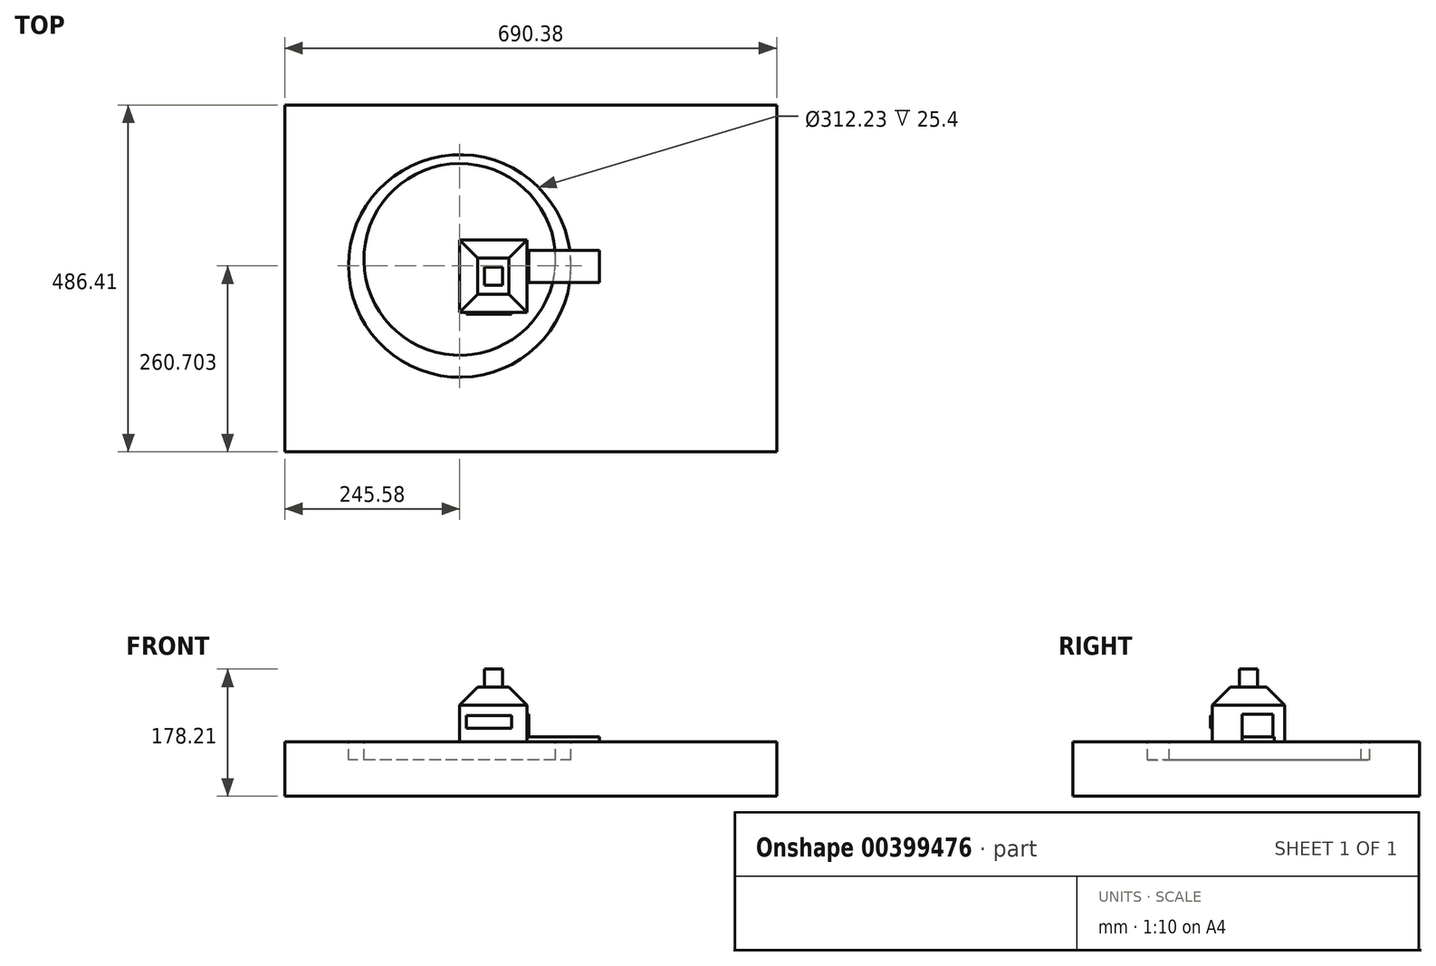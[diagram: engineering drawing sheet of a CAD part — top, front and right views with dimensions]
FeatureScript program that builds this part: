
annotation { "Feature Type Name" : "Feature", "Feature Type Description" : "" }
export const myFeature = defineFeature(function(context is Context, id is Id, definition is map)
    precondition{}
    {
        {
            var Q0;
            Q0=qCreatedBy(makeId("Front.planeOp"),FACE);
            var sketch = newSketch(context, id + "F0", { "sketchPlane" : qUnion([Q0])});
            skLineSegment(sketch, "E0.bottom", {"start": v(0, 0) * mm, "end": v(94.42, 0) * mm});
            skLineSegment(sketch, "E0.top", {"start": v(0, 76.6) * mm, "end": v(94.42, 76.6) * mm});
            skLineSegment(sketch, "E0.left", {"start": v(0, 0) * mm, "end": v(0, 76.6) * mm});
            skLineSegment(sketch, "E0.right", {"start": v(94.42, 0) * mm, "end": v(94.42, 76.6) * mm});
            skSolve(sketch);
        }
        {
            var Q0;
            Q0=makeQuery(id+"F0.imprint","IMPRINT",FACE,{"disambiguationData":[TD([[makeQuery(id+"F0.imprint","IMPRINT",EDGE,{"derivedFrom":sQuery(id+"F0.wireOp",EDGE,"E0.bottom")}),1.0]])]});
            extrude(context, id + "F1", {"entities" : qUnion([Q0]), "depth" : 101.6 * mm});
        }
        {
            var Q0;
            Q0=makeQuery(id+"F1.opExtrude","SWEPT_FACE",FACE,{"disambiguationData":[OSD([sQuery(id+"F0.wireOp",EDGE,"E0.top")])]});
            chamfer(context, id + "F2", {"entities" : qUnion([Q0]), "width" : 25.4 * mm, "tangentPropagation" : true});
        }
        {
            var Q0;
            Q0=makeQuery(id+"F1.opExtrude","SWEPT_FACE",FACE,{"disambiguationData":[OSD([sQuery(id+"F0.wireOp",EDGE,"E0.top")])]});
            var sketch = newSketch(context, id + "F3", { "sketchPlane" : qUnion([Q0])});
            skLineSegment(sketch, "E1.bottom", {"start": v(34.5, -63.5) * mm, "end": v(59.9, -63.5) * mm});
            skLineSegment(sketch, "E1.top", {"start": v(34.5, -38.1) * mm, "end": v(59.9, -38.1) * mm});
            skLineSegment(sketch, "E1.left", {"start": v(34.5, -63.5) * mm, "end": v(34.5, -38.1) * mm});
            skLineSegment(sketch, "E1.right", {"start": v(59.9, -63.5) * mm, "end": v(59.9, -38.1) * mm});
            skSolve(sketch);
        }
        {
            var Q0;
            Q0=makeQuery(id+"F3.imprint","IMPRINT",FACE,{"disambiguationData":[TD([[makeQuery(id+"F3.imprint","IMPRINT",EDGE,{"derivedFrom":sQuery(id+"F3.wireOp",EDGE,"E1.bottom")}),1.0]])]});
            extrude(context, id + "F4", {"entities" : qUnion([Q0]), "operationType" : NewBodyOperationType.ADD, "depth" : 25.4 * mm});
        }
        {
            var Q0;
            Q0=makeQuery(id+"F1.opExtrude","CAP_FACE",FACE,{"disambiguationData":[OSD([sQuery(id+"F0.wireOp",EDGE,"E0.bottom"),sQuery(id+"F0.wireOp",EDGE,"E0.top"),sQuery(id+"F0.wireOp",EDGE,"E0.left"),sQuery(id+"F0.wireOp",EDGE,"E0.right")])],"isStart":false});
            var sketch = newSketch(context, id + "F5", { "sketchPlane" : qUnion([Q0])});
            skLineSegment(sketch, "E2.bottom", {"start": v(9.13, 36.58) * mm, "end": v(72.87, 36.58) * mm});
            skLineSegment(sketch, "E2.top", {"start": v(9.13, 18.94) * mm, "end": v(72.87, 18.94) * mm});
            skLineSegment(sketch, "E2.left", {"start": v(9.13, 36.58) * mm, "end": v(9.13, 18.94) * mm});
            skLineSegment(sketch, "E2.right", {"start": v(72.87, 36.58) * mm, "end": v(72.87, 18.94) * mm});
            skSolve(sketch);
        }
        {
            var Q0;
            Q0=makeQuery(id+"F1.opExtrude","SWEPT_FACE",FACE,{"disambiguationData":[OSD([sQuery(id+"F0.wireOp",EDGE,"E0.right")])]});
            var sketch = newSketch(context, id + "F6", { "sketchPlane" : qUnion([Q0])});
            skLineSegment(sketch, "E3.bottom", {"start": v(-59.73, 0) * mm, "end": v(-14.6, 0) * mm});
            skLineSegment(sketch, "E3.top", {"start": v(-59.73, 6.8) * mm, "end": v(-14.6, 6.8) * mm});
            skLineSegment(sketch, "E3.left", {"start": v(-59.73, 0) * mm, "end": v(-59.73, 6.8) * mm});
            skLineSegment(sketch, "E3.right", {"start": v(-14.6, 0) * mm, "end": v(-14.6, 6.8) * mm});
            skSolve(sketch);
        }
        {
            var Q0;
            Q0=makeQuery(id+"F6.imprint","IMPRINT",FACE,{"disambiguationData":[TD([[makeQuery(id+"F6.imprint","IMPRINT",EDGE,{"derivedFrom":sQuery(id+"F6.wireOp",EDGE,"E3.bottom")}),1.0]])]});
            extrude(context, id + "F7", {"entities" : qUnion([Q0]), "operationType" : NewBodyOperationType.ADD, "depth" : 101.6 * mm});
        }
        {
            var Q0;
            Q0=makeQuery(id+"F5.imprint","IMPRINT",FACE,{"disambiguationData":[TD([[makeQuery(id+"F5.imprint","IMPRINT",EDGE,{"derivedFrom":sQuery(id+"F5.wireOp",EDGE,"E2.bottom")}),-1.0]])]});
            extrude(context, id + "F8", {"entities" : qUnion([Q0]), "operationType" : NewBodyOperationType.ADD, "depth" : 2.54 * mm});
        }
        {
            var Q0;
            Q0=makeQuery(id+"F1.opExtrude","SWEPT_FACE",FACE,{"disambiguationData":[OSD([sQuery(id+"F0.wireOp",EDGE,"E0.right")])]});
            var sketch = newSketch(context, id + "F9", { "sketchPlane" : qUnion([Q0])});
            skLineSegment(sketch, "E4.bottom", {"start": v(-59.73, 6.8) * mm, "end": v(-16.32, 6.8) * mm});
            skLineSegment(sketch, "E4.top", {"start": v(-59.73, 38.95) * mm, "end": v(-16.32, 38.95) * mm});
            skLineSegment(sketch, "E4.left", {"start": v(-59.73, 6.8) * mm, "end": v(-59.73, 38.95) * mm});
            skLineSegment(sketch, "E4.right", {"start": v(-16.32, 6.8) * mm, "end": v(-16.32, 38.95) * mm});
            skSolve(sketch);
        }
        {
            var Q0;
            Q0=makeQuery(id+"F9.imprint","IMPRINT",FACE,{"disambiguationData":[TD([[makeQuery(id+"F9.imprint","IMPRINT",EDGE,{"derivedFrom":sQuery(id+"F9.wireOp",EDGE,"E4.bottom")}),1.0]])]});
            extrude(context, id + "F10", {"entities" : qUnion([Q0]), "operationType" : NewBodyOperationType.ADD, "depth" : 2.54 * mm});
        }
        {
            var Q0;
            Q0=makeQuery(id+"F7.boolean.opBoolean","MERGE",FACE,{"derivedFrom":[makeQuery(id+"F1.opExtrude","SWEPT_FACE",FACE,{"disambiguationData":[OSD([sQuery(id+"F0.wireOp",EDGE,"E0.bottom")])]}),makeQuery(id+"F7.opExtrude","SWEPT_FACE",FACE,{"disambiguationData":[OSD([sQuery(id+"F6.wireOp",EDGE,"E3.bottom")])]})]});
            var sketch = newSketch(context, id + "F11", { "sketchPlane" : qUnion([Q0])});
            skLineSegment(sketch, "E5.bottom", {"start": v(-245.58, 297.2) * mm, "end": v(444.8, 297.2) * mm});
            skLineSegment(sketch, "E5.top", {"start": v(-245.58, -189.22) * mm, "end": v(444.8, -189.22) * mm});
            skLineSegment(sketch, "E5.left", {"start": v(-245.58, 297.2) * mm, "end": v(-245.58, -189.22) * mm});
            skLineSegment(sketch, "E5.right", {"start": v(444.8, 297.2) * mm, "end": v(444.8, -189.22) * mm});
            skSolve(sketch);
        }
        {
            var Q0;
            Q0=makeQuery(id+"F11.imprint","IMPRINT",FACE,{"disambiguationData":[TD([[makeQuery(id+"F11.imprint","IMPRINT",EDGE,{"derivedFrom":sQuery(id+"F11.wireOp",EDGE,"E5.bottom")}),-1.0]])]});
            var Q1;
            {var subQ3=sQuery(id+"F0.wireOp",EDGE,"E0.bottom");Q1=makeQuery(id+"F11.imprint","IMPRINT",FACE,{"disambiguationData":[TD([[makeQuery(id+"F11.imprint","IMPRINT",EDGE,{"derivedFrom":makeQuery(id+"F1.opExtrude","CAP_EDGE",EDGE,{"disambiguationData":[OSD([subQ3])],"isStart":true})}),1.0]])]});}
            extrude(context, id + "F12", {"entities" : qUnion([Q0, Q1]), "operationType" : NewBodyOperationType.ADD, "depth" : 76.2 * mm});
        }
        {
            var Q0;
            Q0=makeQuery(id+"F12.opExtrude","CAP_FACE",FACE,{"disambiguationData":[OSD([sQuery(id+"F11.wireOp",EDGE,"E5.bottom"),sQuery(id+"F11.wireOp",EDGE,"E5.top"),sQuery(id+"F11.wireOp",EDGE,"E5.left"),sQuery(id+"F11.wireOp",EDGE,"E5.right")])],"isStart":true});
            var sketch = newSketch(context, id + "F13", { "sketchPlane" : qUnion([Q0])});
            skLineSegment(sketch, "E6.bottom", {"start": v(444.8, -297.2) * mm, "end": v(194.55, -297.2) * mm});
            skLineSegment(sketch, "E6.top", {"start": v(444.8, 189.22) * mm, "end": v(194.55, 189.22) * mm});
            skLineSegment(sketch, "E6.left", {"start": v(444.8, -297.2) * mm, "end": v(444.8, 189.22) * mm});
            skLineSegment(sketch, "E6.right", {"start": v(194.55, -297.2) * mm, "end": v(194.55, 189.22) * mm});
            skSolve(sketch);
        }
        {
            var Q0;
            {var subQ11=makeQuery(id+"F12.opExtrude","CAP_EDGE",EDGE,{"disambiguationData":[OSD([sQuery(id+"F11.wireOp",EDGE,"E5.left")])],"isStart":true});Q0=makeQuery(id+"F13.imprint","IMPRINT",FACE,{"disambiguationData":[TD([[makeQuery(id+"F13.imprint","IMPRINT",EDGE,{"derivedFrom":subQ11}),-1.0]])]});}
            var sketch = newSketch(context, id + "F14", { "sketchPlane" : qUnion([Q0])});
            skCircle(sketch, "E7", {"center": v(0, -36.49) * mm, "radius": 156.11 * mm});
            skSolve(sketch);
        }
        {
            var Q0;
            Q0 = qSketchRegion(id + "F14", true);
            extrude(context, id + "F15", {"entities" : qUnion([Q0]), "operationType" : NewBodyOperationType.REMOVE, "oppositeDirection" : true, "depth" : 25.4 * mm});
        }
        {
            var Q0;
            {var subQ11=makeQuery(id+"F12.opExtrude","CAP_EDGE",EDGE,{"disambiguationData":[OSD([sQuery(id+"F11.wireOp",EDGE,"E5.left")])],"isStart":true});Q0=makeQuery(id+"F13.imprint","IMPRINT",FACE,{"disambiguationData":[TD([[makeQuery(id+"F13.imprint","IMPRINT",EDGE,{"derivedFrom":subQ11}),-1.0]])]});}
            var sketch = newSketch(context, id + "F16", { "sketchPlane" : qUnion([Q0])});
            skCircle(sketch, "E8", {"center": v(0, -27.2) * mm, "radius": 134.47 * mm});
            skSolve(sketch);
        }
        {
            var Q0;
            Q0 = qSketchRegion(id + "F16", true);
            var Q1;
            Q1=makeQuery(id+"F15.boolean.opBoolean","COPY",FACE,{"derivedFrom":makeQuery(id+"F15.opExtrude","CAP_FACE",FACE,{"disambiguationData":[OSD([sQuery(id+"F14.wireOp",EDGE,"E7")])],"isStart":false})});
            extrude(context, id + "F17", {"entities" : qUnion([Q0]), "operationType" : NewBodyOperationType.ADD, "endBound" : BoundingType.UP_TO_SURFACE, "oppositeDirection" : true, "endBoundEntityFace" : qUnion([Q1]), "depth" : 25.4 * mm});
        }
    });
